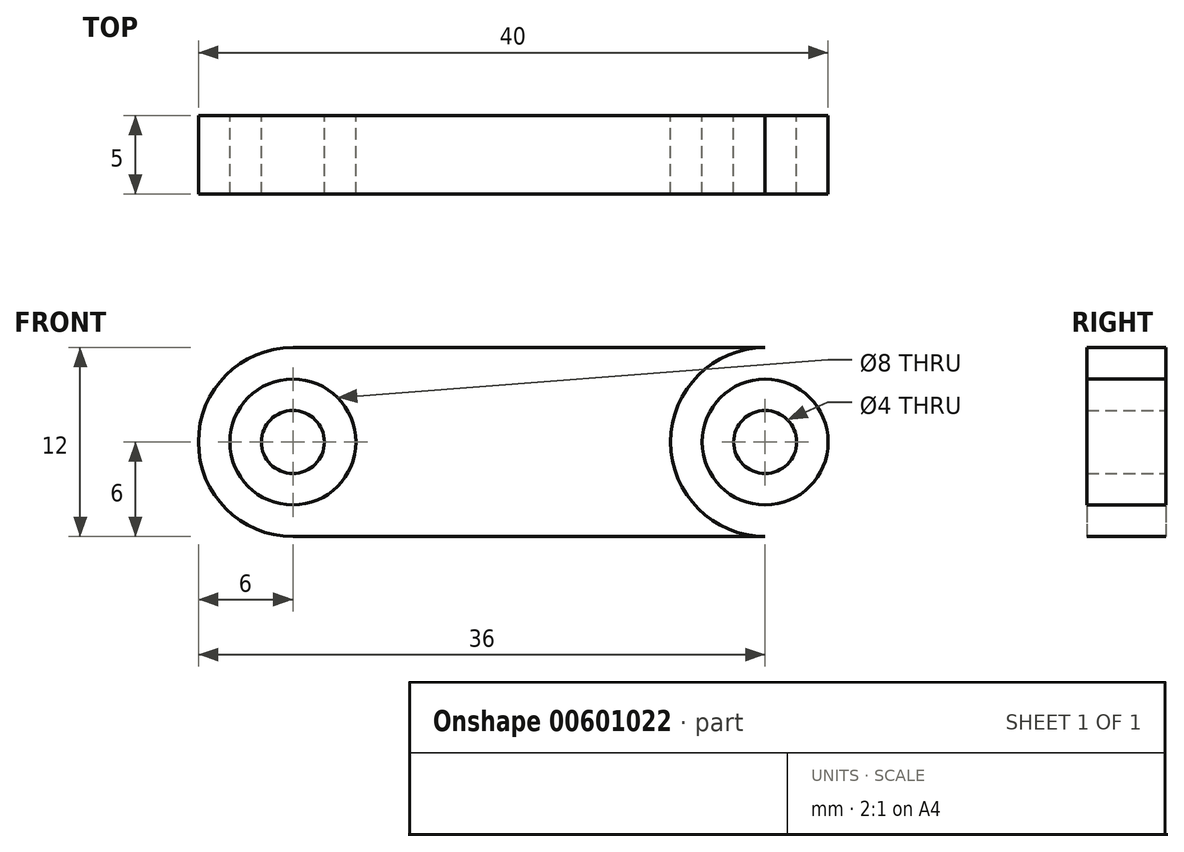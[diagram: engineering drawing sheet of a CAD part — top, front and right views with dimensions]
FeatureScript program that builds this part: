
annotation { "Feature Type Name" : "Feature", "Feature Type Description" : "" }
export const myFeature = defineFeature(function(context is Context, id is Id, definition is map)
    precondition{}
    {
        {
            var Q0;
            Q0=qCreatedBy(makeId("Front.planeOp"),FACE);
            var sketch = newSketch(context, id + "F0", { "sketchPlane" : qUnion([Q0])});
            skCircle(sketch, "E0", {"center": v(-15, 0) * mm, "radius": 6 * mm});
            skCircle(sketch, "E1", {"center": v(-15, 0) * mm, "radius": 4 * mm});
            skCircle(sketch, "E2", {"center": v(-15, 0) * mm, "radius": 2 * mm});
            skLineSegment(sketch, "E3", {"start": v(-15, 6) * mm, "end": v(0, 6) * mm});
            skLineSegment(sketch, "E4", {"start": v(-15.03, -6) * mm, "end": v(0, -6) * mm});
            skCircle(sketch, "E5.MirrorC", {"center": v(15, 0) * mm, "radius": 6 * mm});
            skCircle(sketch, "E6.MirrorC", {"center": v(15, 0) * mm, "radius": 4 * mm});
            skLineSegment(sketch, "E7.MirrorCS", {"start": v(15.03, -6) * mm, "end": v(0, -6) * mm});
            skLineSegment(sketch, "E8.MirrorCS", {"start": v(15, 6) * mm, "end": v(0, 6) * mm});
            skCircle(sketch, "E9.MirrorC", {"center": v(15, 0) * mm, "radius": 2 * mm});
            skSolve(sketch);
        }
        {
            var Q0;
            Q0=makeQuery(id+"F0.imprint","IMPRINT",FACE,{"disambiguationData":[TD([[makeQuery(id+"F0.imprint","IMPRINT",EDGE,{"derivedFrom":sQuery(id+"F0.wireOp",EDGE,"E2")}),1.0]])]});
            var Q1;
            Q1=makeQuery(id+"F0.imprint","IMPRINT",FACE,{"disambiguationData":[TD([[makeQuery(id+"F0.imprint","IMPRINT",EDGE,{"derivedFrom":sQuery(id+"F0.wireOp",EDGE,"E1")}),-1.0]])]});
            var Q2;
            {var subQ4=sQuery(id+"F0.wireOp",EDGE,"E3");Q2=makeQuery(id+"F0.imprint","IMPRINT",FACE,{"disambiguationData":[TD([[makeQuery(id+"F0.imprint","IMPRINT",EDGE,{"derivedFrom":subQ4}),-1.0]])]});}
            var Q3;
            Q3=makeQuery(id+"F0.imprint","IMPRINT",FACE,{"disambiguationData":[TD([[makeQuery(id+"F0.imprint","IMPRINT",EDGE,{"derivedFrom":sQuery(id+"F0.wireOp",EDGE,"E6.MirrorC")}),1.0]])]});
            var Q4;
            Q4=makeQuery(id+"F0.imprint","IMPRINT",FACE,{"disambiguationData":[TD([[makeQuery(id+"F0.imprint","IMPRINT",EDGE,{"derivedFrom":sQuery(id+"F0.wireOp",EDGE,"E9.MirrorC")}),-1.0]])]});
            extrude(context, id + "F1", {"entities" : qUnion([Q0, Q1, Q2, Q3, Q4]), "depth" : 5 * mm, "offsetDistance" : 25 * mm});
        }
    });
